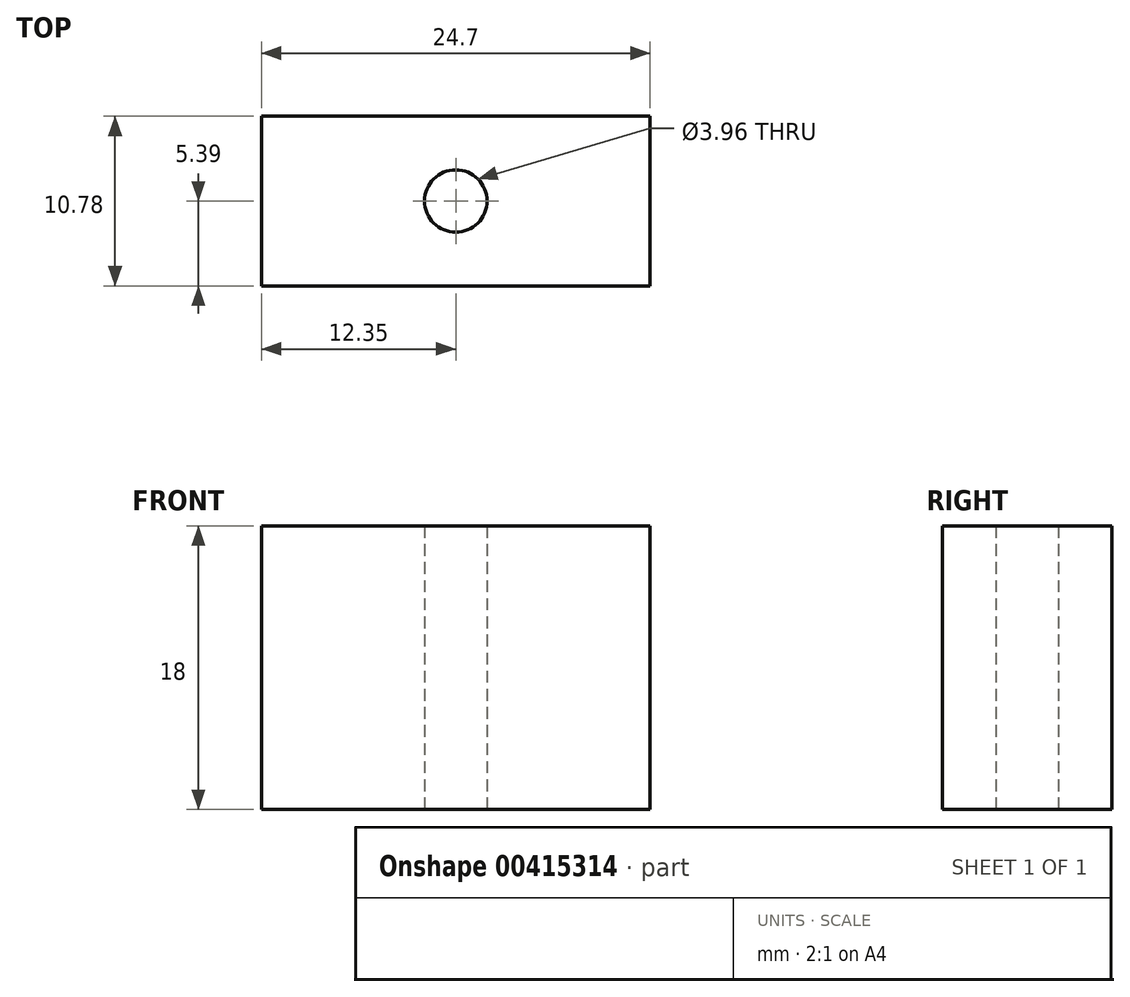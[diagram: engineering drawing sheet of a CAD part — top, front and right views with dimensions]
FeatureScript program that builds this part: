
annotation { "Feature Type Name" : "Feature", "Feature Type Description" : "" }
export const myFeature = defineFeature(function(context is Context, id is Id, definition is map)
    precondition{}
    {
        {
            var Q0;
            Q0=qCreatedBy(makeId("Top.planeOp"),FACE);
            var sketch = newSketch(context, id + "F0", { "sketchPlane" : qUnion([Q0])});
            skLineSegment(sketch, "E0.bottom", {"start": v(12.35, -5.39) * mm, "end": v(-12.35, -5.4) * mm});
            skLineSegment(sketch, "E0.top", {"start": v(12.35, 5.4) * mm, "end": v(-12.35, 5.39) * mm});
            skLineSegment(sketch, "E0.left", {"start": v(12.35, -5.4) * mm, "end": v(12.35, 5.39) * mm});
            skLineSegment(sketch, "E0.right", {"start": v(-12.35, -5.4) * mm, "end": v(-12.35, 5.39) * mm});
            skPoint(sketch, "E0.middle", {"position": v(0, 0) * mm});
            skLineSegment(sketch, "E1.bottom", {"start": v(-17.35, -8.4) * mm, "end": v(17.35, -8.4) * mm});
            skLineSegment(sketch, "E1.top", {"start": v(-17.35, 8.4) * mm, "end": v(17.35, 8.4) * mm});
            skLineSegment(sketch, "E1.left", {"start": v(-17.35, -8.4) * mm, "end": v(-17.35, 8.4) * mm});
            skLineSegment(sketch, "E1.right", {"start": v(17.35, -8.4) * mm, "end": v(17.35, 8.4) * mm});
            skCircle(sketch, "E2", {"center": v(0, 0) * mm, "radius": 1.58 * mm});
            skCircle(sketch, "E3", {"center": v(0, 0) * mm, "radius": 1.98 * mm});
            skSolve(sketch);
        }
        {
            var Q0;
            Q0=makeQuery(id+"F0.imprint","IMPRINT",FACE,{"disambiguationData":[TD([[makeQuery(id+"F0.imprint","IMPRINT",EDGE,{"derivedFrom":sQuery(id+"F0.wireOp",EDGE,"E0.bottom")}),-1.0]])]});
            extrude(context, id + "F1", {"entities" : qUnion([Q0]), "depth" : 18 * mm});
        }
    });
